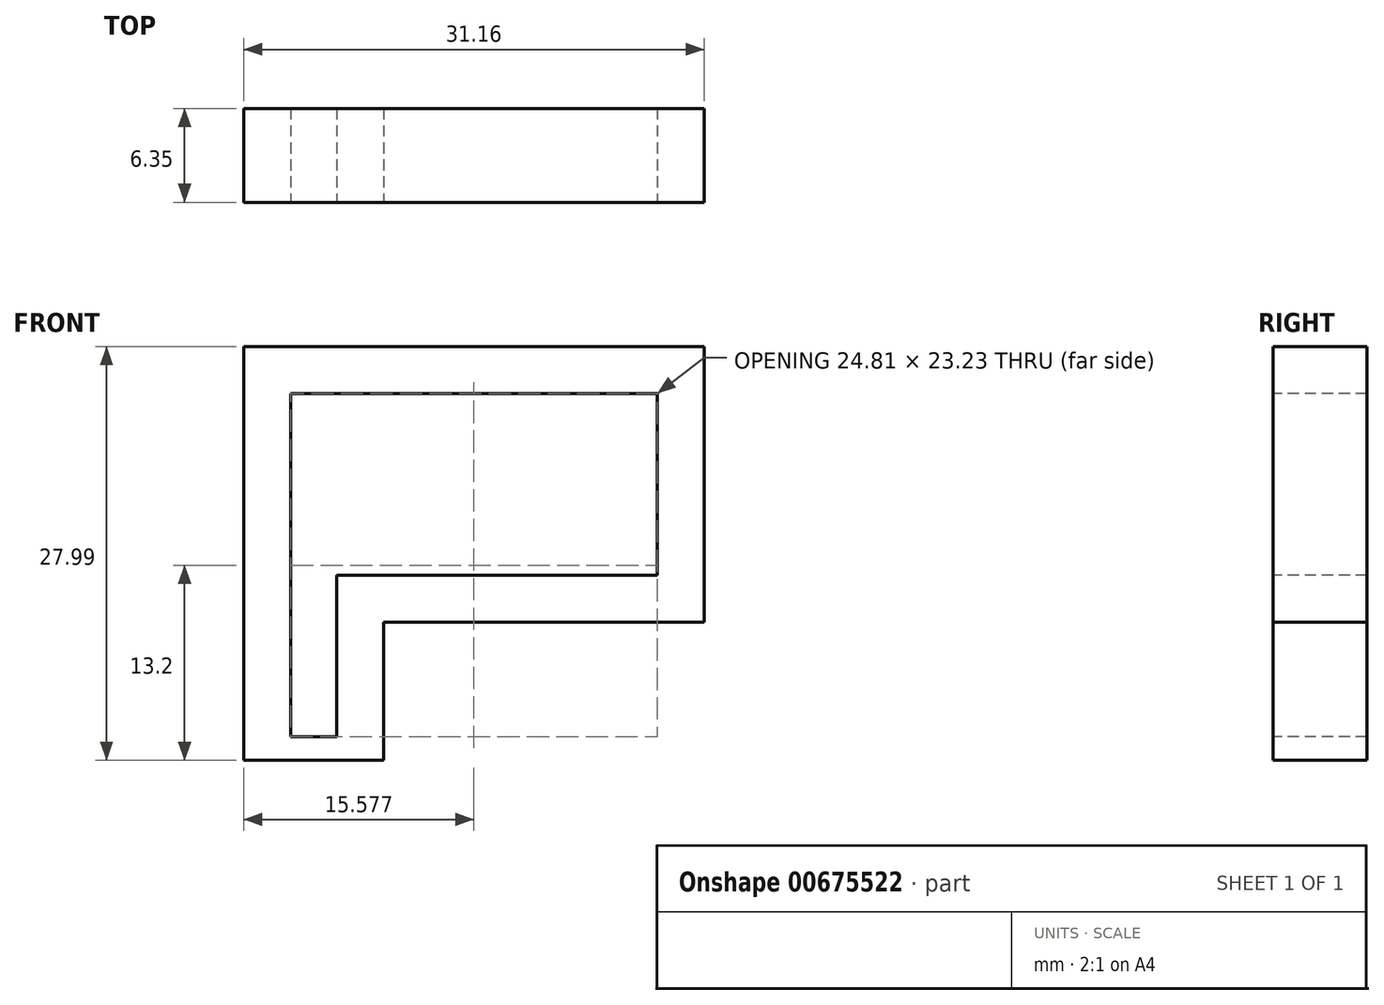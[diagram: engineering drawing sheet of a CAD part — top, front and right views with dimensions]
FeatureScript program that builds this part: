
annotation { "Feature Type Name" : "Feature", "Feature Type Description" : "" }
export const myFeature = defineFeature(function(context is Context, id is Id, definition is map)
    precondition{}
    {
        {
            var Q0;
            Q0=qCreatedBy(makeId("Top.planeOp"),FACE);
            var sketch = newSketch(context, id + "F0", { "sketchPlane" : qUnion([Q0])});
            skLineSegment(sketch, "E0.bottom", {"start": v(-11.25, 0.68) * mm, "end": v(18.9, 0.68) * mm});
            skLineSegment(sketch, "E0.top", {"start": v(-11.25, -5.67) * mm, "end": v(18.9, -5.67) * mm});
            skLineSegment(sketch, "E0.left", {"start": v(-11.25, 0.68) * mm, "end": v(-11.25, -5.67) * mm});
            skLineSegment(sketch, "E0.right", {"start": v(18.9, 0.68) * mm, "end": v(18.9, -5.67) * mm});
            skSolve(sketch);
        }
        {
            var Q0;
            Q0 = qSketchRegion(id + "F0", true);
            extrude(context, id + "F1", {"entities" : qUnion([Q0]), "depth" : 26.99 * mm, "offsetDistance" : 25.4 * mm});
        }
        {
            var Q0;
            Q0=makeQuery(id+"F1.opExtrude","SWEPT_FACE",FACE,{"disambiguationData":[OSD([sQuery(id+"F0.wireOp",EDGE,"E0.top")])]});
            var sketch = newSketch(context, id + "F2", { "sketchPlane" : qUnion([Q0])});
            skLineSegment(sketch, "E1", {"start": v(-11.25, 0) * mm, "end": v(-8.08, 0) * mm, "construction": true});
            skLineSegment(sketch, "E2", {"start": v(18.9, 0) * mm, "end": v(15.73, 0) * mm, "construction": true});
            skLineSegment(sketch, "E3", {"start": v(15.73, 0) * mm, "end": v(15.73, 9.52) * mm, "construction": true});
            skLineSegment(sketch, "E4", {"start": v(15.73, 23.81) * mm, "end": v(-8.08, 23.81) * mm});
            skLineSegment(sketch, "E5", {"start": v(-8.08, 0) * mm, "end": v(-8.08, 1.59) * mm, "construction": true});
            skLineSegment(sketch, "E6", {"start": v(15.73, 9.52) * mm, "end": v(15.73, 23.81) * mm});
            skLineSegment(sketch, "E7", {"start": v(-8.08, 1.59) * mm, "end": v(-8.08, 23.81) * mm});
            skLineSegment(sketch, "E8", {"start": v(-8.08, 1.59) * mm, "end": v(-4.9, 1.59) * mm});
            skLineSegment(sketch, "E9", {"start": v(-4.9, 1.59) * mm, "end": v(-4.9, 0) * mm});
            skLineSegment(sketch, "E10", {"start": v(15.73, 9.52) * mm, "end": v(3.03, 9.52) * mm});
            skLineSegment(sketch, "E11", {"start": v(3.03, 9.52) * mm, "end": v(3.03, 0) * mm});
            skLineSegment(sketch, "E12", {"start": v(3.03, 0) * mm, "end": v(-4.9, 0) * mm});
            skSolve(sketch);
        }
        {
            var Q0;
            Q0 = qSketchRegion(id + "F2", true);
            extrude(context, id + "F3", {"entities" : qUnion([Q0]), "operationType" : NewBodyOperationType.REMOVE, "endBound" : BoundingType.THROUGH_ALL, "oppositeDirection" : true, "depth" : 25.4 * mm, "offsetDistance" : 25.4 * mm});
        }
        {
            var Q0;
            Q0=makeQuery(id+"F1.opExtrude","SWEPT_FACE",FACE,{"disambiguationData":[OSD([sQuery(id+"F0.wireOp",EDGE,"E0.top")])]});
            var sketch = newSketch(context, id + "F4", { "sketchPlane" : qUnion([Q0])});
            skLineSegment(sketch, "E13", {"start": v(3.03, 0) * mm, "end": v(6.2, 0) * mm, "construction": true});
            skLineSegment(sketch, "E14", {"start": v(6.2, 0) * mm, "end": v(6.2, 6.35) * mm});
            skLineSegment(sketch, "E15", {"start": v(6.2, 6.35) * mm, "end": v(18.9, 6.35) * mm});
            skLineSegment(sketch, "E16", {"start": v(6.2, 0) * mm, "end": v(18.9, 0) * mm});
            skLineSegment(sketch, "E17", {"start": v(18.9, 0) * mm, "end": v(18.9, 6.35) * mm});
            skSolve(sketch);
        }
        {
            var Q0;
            Q0 = qSketchRegion(id + "F4", true);
            extrude(context, id + "F5", {"entities" : qUnion([Q0]), "operationType" : NewBodyOperationType.REMOVE, "endBound" : BoundingType.THROUGH_ALL, "oppositeDirection" : true, "depth" : 25.4 * mm, "offsetDistance" : 25.4 * mm});
        }
        {
            var Q0;
            Q0=makeQuery(id+"F3.boolean.opBoolean","COPY",FACE,{"derivedFrom":makeQuery(id+"F3.opExtrude","SWEPT_FACE",FACE,{"disambiguationData":[OSD([sQuery(id+"F2.wireOp",EDGE,"E9")])]})});
            var sketch = newSketch(context, id + "F6", { "sketchPlane" : qUnion([Q0])});
            skLineSegment(sketch, "E18.bottom", {"start": v(-5.67, 0) * mm, "end": v(0.68, 0) * mm});
            skLineSegment(sketch, "E18.top", {"start": v(-5.67, 1.59) * mm, "end": v(0.68, 1.59) * mm});
            skLineSegment(sketch, "E18.left", {"start": v(-5.67, 0) * mm, "end": v(-5.67, 1.59) * mm});
            skLineSegment(sketch, "E18.right", {"start": v(0.68, 0) * mm, "end": v(0.68, 1.59) * mm});
            skSolve(sketch);
        }
        {
            var Q0;
            Q0 = qSketchRegion(id + "F6", true);
            extrude(context, id + "F7", {"entities" : qUnion([Q0]), "operationType" : NewBodyOperationType.ADD, "depth" : 7.94 * mm, "offsetDistance" : 25.4 * mm});
        }
        {
            var Q0;
            Q0=makeQuery(id+"F3.boolean.opBoolean","COPY",FACE,{"derivedFrom":makeQuery(id+"F3.opExtrude","SWEPT_FACE",FACE,{"disambiguationData":[OSD([sQuery(id+"F2.wireOp",EDGE,"E10")])]})});
            var sketch = newSketch(context, id + "F8", { "sketchPlane" : qUnion([Q0])});
            skLineSegment(sketch, "E19.bottom", {"start": v(3.03, 0.68) * mm, "end": v(15.73, 0.68) * mm});
            skLineSegment(sketch, "E19.top", {"start": v(3.03, -5.67) * mm, "end": v(15.73, -5.67) * mm});
            skLineSegment(sketch, "E19.left", {"start": v(3.03, 0.68) * mm, "end": v(3.03, -5.67) * mm});
            skLineSegment(sketch, "E19.right", {"start": v(15.73, 0.68) * mm, "end": v(15.73, -5.67) * mm});
            skSolve(sketch);
        }
        {
            var Q0;
            Q0 = qSketchRegion(id + "F8", true);
            extrude(context, id + "F9", {"entities" : qUnion([Q0]), "operationType" : NewBodyOperationType.ADD, "depth" : 3 * mm, "offsetDistance" : 25.4 * mm});
        }
        {
            var Q0;
            Q0=makeQuery(id+"F5.boolean.opBoolean","COPY",FACE,{"derivedFrom":makeQuery(id+"F5.opExtrude","SWEPT_FACE",FACE,{"disambiguationData":[OSD([sQuery(id+"F4.wireOp",EDGE,"E15")])]})});
            var sketch = newSketch(context, id + "F10", { "sketchPlane" : qUnion([Q0])});
            skLineSegment(sketch, "E20.bottom", {"start": v(6.2, 5.67) * mm, "end": v(18.9, 5.67) * mm});
            skLineSegment(sketch, "E20.top", {"start": v(6.2, -0.68) * mm, "end": v(18.9, -0.68) * mm});
            skLineSegment(sketch, "E20.left", {"start": v(6.2, 5.67) * mm, "end": v(6.2, -0.68) * mm});
            skLineSegment(sketch, "E20.right", {"start": v(18.9, 5.67) * mm, "end": v(18.9, -0.68) * mm});
            skSolve(sketch);
        }
        {
            var Q0;
            Q0 = qSketchRegion(id + "F10", true);
            extrude(context, id + "F11", {"entities" : qUnion([Q0]), "operationType" : NewBodyOperationType.REMOVE, "oppositeDirection" : true, "depth" : 3 * mm, "offsetDistance" : 25.4 * mm});
        }
        {
            var Q0;
            Q0=makeQuery(id+"F9.boolean.opBoolean","MERGE",FACE,{"derivedFrom":[makeQuery(id+"F3.boolean.opBoolean","COPY",FACE,{"derivedFrom":makeQuery(id+"F3.opExtrude","SWEPT_FACE",FACE,{"disambiguationData":[OSD([sQuery(id+"F2.wireOp",EDGE,"E11")])]})}),makeQuery(id+"F9.opExtrude","SWEPT_FACE",FACE,{"disambiguationData":[OSD([sQuery(id+"F8.wireOp",EDGE,"E19.left")])]})]});
            var sketch = newSketch(context, id + "F12", { "sketchPlane" : qUnion([Q0])});
            skLineSegment(sketch, "E21.bottom", {"start": v(-0.68, 12.52) * mm, "end": v(5.67, 12.52) * mm});
            skLineSegment(sketch, "E21.top", {"start": v(-0.68, 1.59) * mm, "end": v(5.67, 1.59) * mm});
            skLineSegment(sketch, "E21.left", {"start": v(-0.68, 12.52) * mm, "end": v(-0.68, 1.59) * mm});
            skLineSegment(sketch, "E21.right", {"start": v(5.67, 12.52) * mm, "end": v(5.67, 1.59) * mm});
            skSolve(sketch);
        }
        {
            var Q0;
            Q0 = qSketchRegion(id + "F12", true);
            extrude(context, id + "F13", {"entities" : qUnion([Q0]), "operationType" : NewBodyOperationType.ADD, "depth" : 8 * mm, "offsetDistance" : 25.4 * mm});
        }
        {
            var Q0;
            Q0=makeQuery(id+"F11.boolean.opBoolean","MERGE",FACE,{"derivedFrom":[makeQuery(id+"F5.boolean.opBoolean","COPY",FACE,{"derivedFrom":makeQuery(id+"F5.opExtrude","SWEPT_FACE",FACE,{"disambiguationData":[OSD([sQuery(id+"F4.wireOp",EDGE,"E14")])]})}),makeQuery(id+"F11.opExtrude","SWEPT_FACE",FACE,{"disambiguationData":[OSD([sQuery(id+"F10.wireOp",EDGE,"E20.left")])]})]});
            var sketch = newSketch(context, id + "F14", { "sketchPlane" : qUnion([Q0])});
            skLineSegment(sketch, "E22.bottom", {"start": v(-5.67, 9.35) * mm, "end": v(0.68, 9.35) * mm});
            skLineSegment(sketch, "E22.top", {"start": v(-5.67, 0) * mm, "end": v(0.68, 0) * mm});
            skLineSegment(sketch, "E22.left", {"start": v(-5.67, 9.35) * mm, "end": v(-5.67, 0) * mm});
            skLineSegment(sketch, "E22.right", {"start": v(0.68, 9.35) * mm, "end": v(0.68, 0) * mm});
            skSolve(sketch);
        }
        {
            var Q0;
            Q0 = qSketchRegion(id + "F14", true);
            extrude(context, id + "F15", {"entities" : qUnion([Q0]), "operationType" : NewBodyOperationType.REMOVE, "oppositeDirection" : true, "depth" : 8 * mm, "offsetDistance" : 25.4 * mm});
        }
        {
            var Q0;
            Q0=makeQuery(id+"F1.opExtrude","SWEPT_FACE",FACE,{"disambiguationData":[OSD([sQuery(id+"F0.wireOp",EDGE,"E0.right")])]});
            var sketch = newSketch(context, id + "F16", { "sketchPlane" : qUnion([Q0])});
            skLineSegment(sketch, "E23.bottom", {"start": v(-5.67, 26.99) * mm, "end": v(0.68, 26.99) * mm});
            skLineSegment(sketch, "E23.top", {"start": v(-5.67, 9.35) * mm, "end": v(0.68, 9.35) * mm});
            skLineSegment(sketch, "E23.left", {"start": v(-5.67, 26.99) * mm, "end": v(-5.67, 9.35) * mm});
            skLineSegment(sketch, "E23.right", {"start": v(0.68, 26.99) * mm, "end": v(0.68, 9.35) * mm});
            skSolve(sketch);
        }
        {
            var Q0;
            Q0 = qSketchRegion(id + "F16", true);
            extrude(context, id + "F17", {"entities" : qUnion([Q0]), "operationType" : NewBodyOperationType.ADD, "depth" : 1 * mm, "offsetDistance" : 25.4 * mm});
        }
        {
            var Q0;
            Q0=makeQuery(id+"F3.boolean.opBoolean","COPY",FACE,{"derivedFrom":makeQuery(id+"F3.opExtrude","SWEPT_FACE",FACE,{"disambiguationData":[OSD([sQuery(id+"F2.wireOp",EDGE,"E6")])]})});
            var sketch = newSketch(context, id + "F18", { "sketchPlane" : qUnion([Q0])});
            skLineSegment(sketch, "E24.bottom", {"start": v(5.67, 12.52) * mm, "end": v(-0.68, 12.52) * mm});
            skLineSegment(sketch, "E24.top", {"start": v(5.67, 23.81) * mm, "end": v(-0.68, 23.81) * mm});
            skLineSegment(sketch, "E24.left", {"start": v(5.67, 12.52) * mm, "end": v(5.67, 23.81) * mm});
            skLineSegment(sketch, "E24.right", {"start": v(-0.68, 12.52) * mm, "end": v(-0.68, 23.81) * mm});
            skSolve(sketch);
        }
        {
            var Q0;
            Q0 = qSketchRegion(id + "F18", true);
            extrude(context, id + "F19", {"entities" : qUnion([Q0]), "operationType" : NewBodyOperationType.REMOVE, "oppositeDirection" : true, "depth" : 1 * mm, "offsetDistance" : 25.4 * mm});
        }
        {
            var Q0;
            Q0=makeQuery(id+"F19.boolean.opBoolean","MERGE",FACE,{"derivedFrom":[makeQuery(id+"F3.boolean.opBoolean","COPY",FACE,{"derivedFrom":makeQuery(id+"F3.opExtrude","SWEPT_FACE",FACE,{"disambiguationData":[OSD([sQuery(id+"F2.wireOp",EDGE,"E4")])]})}),makeQuery(id+"F19.opExtrude","SWEPT_FACE",FACE,{"disambiguationData":[OSD([sQuery(id+"F18.wireOp",EDGE,"E24.top")])]})]});
            var sketch = newSketch(context, id + "F20", { "sketchPlane" : qUnion([Q0])});
            skLineSegment(sketch, "E25.bottom", {"start": v(16.73, 5.67) * mm, "end": v(-8.08, 5.67) * mm});
            skLineSegment(sketch, "E25.top", {"start": v(16.73, -0.68) * mm, "end": v(-8.08, -0.68) * mm});
            skLineSegment(sketch, "E25.left", {"start": v(16.73, 5.67) * mm, "end": v(16.73, -0.68) * mm});
            skLineSegment(sketch, "E25.right", {"start": v(-8.08, 5.67) * mm, "end": v(-8.08, -0.68) * mm});
            skSolve(sketch);
        }
        {
            var Q0;
            Q0 = qSketchRegion(id + "F20", true);
            extrude(context, id + "F21", {"entities" : qUnion([Q0]), "operationType" : NewBodyOperationType.REMOVE, "oppositeDirection" : true, "depth" : 1 * mm, "offsetDistance" : 25.4 * mm});
        }
        {
            var Q0;
            Q0=makeQuery(id+"F17.boolean.opBoolean","MERGE",FACE,{"derivedFrom":[makeQuery(id+"F1.opExtrude","CAP_FACE",FACE,{"disambiguationData":[OSD([sQuery(id+"F0.wireOp",EDGE,"E0.bottom"),sQuery(id+"F0.wireOp",EDGE,"E0.top"),sQuery(id+"F0.wireOp",EDGE,"E0.left"),sQuery(id+"F0.wireOp",EDGE,"E0.right")])],"isStart":false}),makeQuery(id+"F17.opExtrude","SWEPT_FACE",FACE,{"disambiguationData":[OSD([sQuery(id+"F16.wireOp",EDGE,"E23.bottom")])]})]});
            var sketch = newSketch(context, id + "F22", { "sketchPlane" : qUnion([Q0])});
            skLineSegment(sketch, "E26.bottom", {"start": v(19.9, 0.68) * mm, "end": v(-11.25, 0.68) * mm});
            skLineSegment(sketch, "E26.top", {"start": v(19.9, -5.67) * mm, "end": v(-11.25, -5.67) * mm});
            skLineSegment(sketch, "E26.left", {"start": v(19.9, 0.68) * mm, "end": v(19.9, -5.67) * mm});
            skLineSegment(sketch, "E26.right", {"start": v(-11.25, 0.68) * mm, "end": v(-11.25, -5.67) * mm});
            skSolve(sketch);
        }
        {
            var Q0;
            Q0 = qSketchRegion(id + "F22", true);
            extrude(context, id + "F23", {"entities" : qUnion([Q0]), "operationType" : NewBodyOperationType.ADD, "depth" : 1 * mm, "offsetDistance" : 25.4 * mm});
        }
    });
